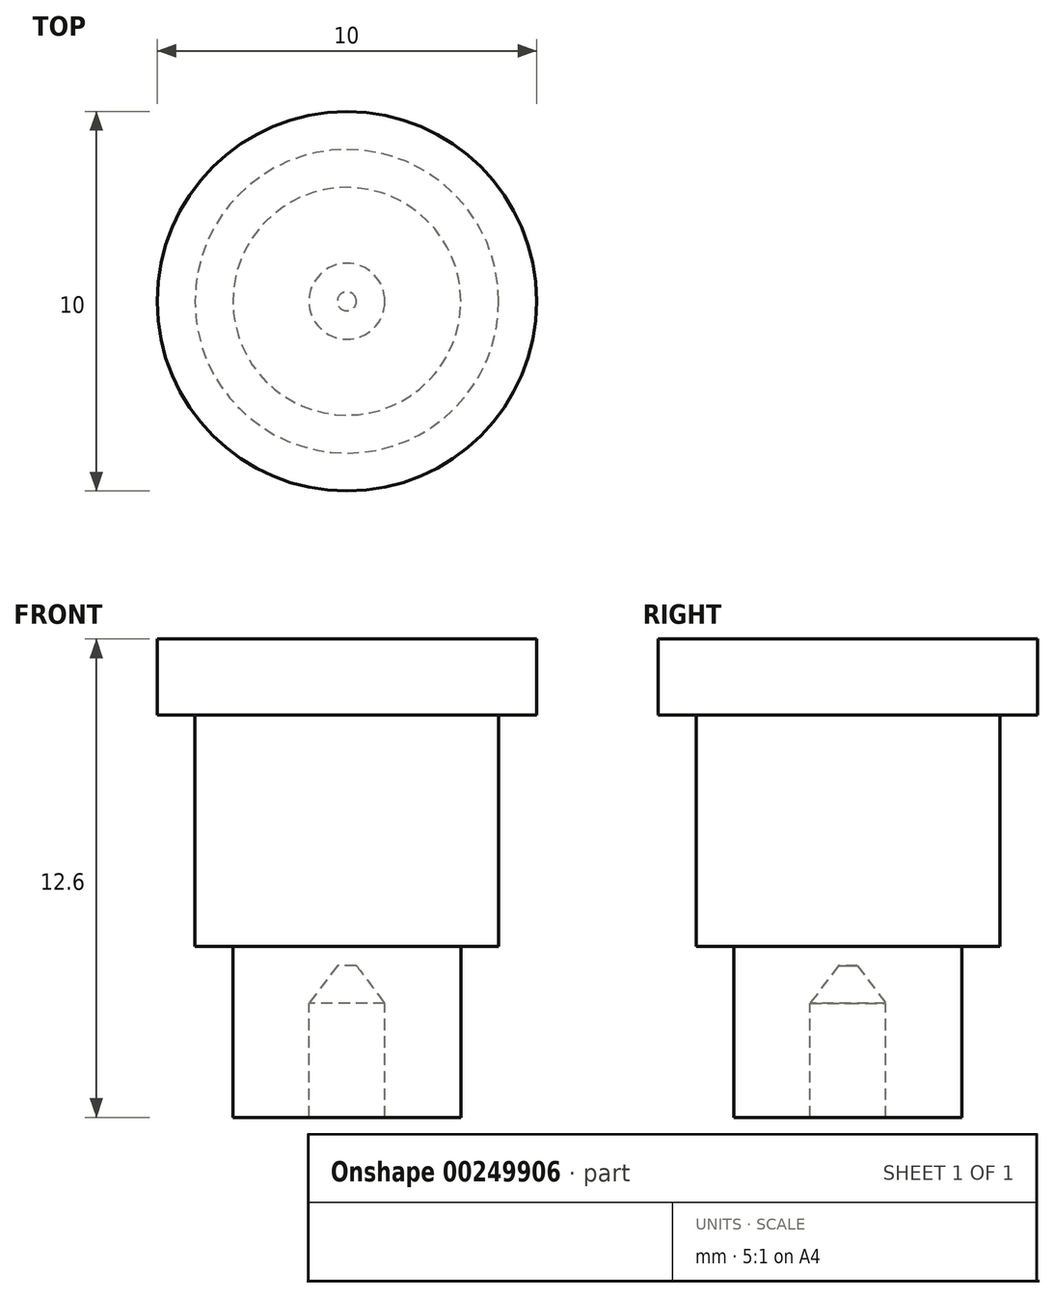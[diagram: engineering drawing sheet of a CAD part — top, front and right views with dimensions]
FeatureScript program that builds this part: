
annotation { "Feature Type Name" : "Feature", "Feature Type Description" : "" }
export const myFeature = defineFeature(function(context is Context, id is Id, definition is map)
    precondition{}
    {
        {
            var Q0;
            Q0=qCreatedBy(makeId("Front.planeOp"),FACE);
            var sketch = newSketch(context, id + "F0", { "sketchPlane" : qUnion([Q0])});
            skLineSegment(sketch, "E0", {"start": v(0, 8.1) * mm, "end": v(-5, 8.1) * mm});
            skLineSegment(sketch, "E1", {"start": v(-5, 8.1) * mm, "end": v(-5, 6.1) * mm});
            skLineSegment(sketch, "E2", {"start": v(-5, 6.1) * mm, "end": v(0, 6.1) * mm});
            skLineSegment(sketch, "E3", {"start": v(-4, 6.1) * mm, "end": v(-4, 0) * mm});
            skLineSegment(sketch, "E4", {"start": v(-4, 0) * mm, "end": v(0, 0) * mm});
            skLineSegment(sketch, "E5", {"start": v(-3, 0) * mm, "end": v(-3, -4.5) * mm});
            skLineSegment(sketch, "E6", {"start": v(-3, -4.5) * mm, "end": v(-1, -4.5) * mm});
            skLineSegment(sketch, "E7", {"start": v(-1, -4.5) * mm, "end": v(-1, -1.5) * mm});
            skLineSegment(sketch, "E8", {"start": v(0, 8.1) * mm, "end": v(0, -0.5) * mm});
            skLineSegment(sketch, "E9", {"start": v(0, -0.5) * mm, "end": v(-0.25, -0.5) * mm});
            skLineSegment(sketch, "E10", {"start": v(-1, -1.5) * mm, "end": v(-0.25, -0.5) * mm});
            skSolve(sketch);
        }
        {
            var Q0;
            Q0 = qSketchRegion(id + "F0", true);
            var Q1;
            Q1=sQuery(id+"F0.wireOp",EDGE,"E8");
            revolve(context, id + "F1", {"entities" : qUnion([Q0]), "axis" : qUnion([Q1]), "revolveType" : RevolveType.FULL});
        }
    });
